# Revit family: DC_Holyoake_OutsideLouver_OHL-C-45_supply_13
name_source: partatom
category: Air Terminals
revit_build: Autodesk Revit 2014 (Build: 20130308_1515(x64)
units: mm (PartAtom-declared; Revit-internal decimal feet)

## types (1)
- OHL-C-45
    Accessories = Aluminium Bird mesh or insect mesh (fibreglass)
    Blade Array Count = 7.68
    Blade Count = 7
    Blade Cut Setout = 350 mm  [stored 1.14829 ft]
    Blade Height = 61.6 mm  [stored 0.2021 ft]
    Blade Length = 354 mm  [stored 1.16142 ft]
    Blade Offset = 3 mm  [stored 0.00984252 ft]
    Blade Pitch = 50 mm  [stored 0.164042 ft]
    Blade Setout = 384 mm
    Blade Width = 44.8 mm  [stored 0.146982 ft]
    Channel Thickness = 50.8 mm  [stored 0.166667 ft]
    Channel Width = 25.4 mm  [stored 0.0833333 ft]
    Description = Weather Louvres shall be Holyoake Model OHL-C-45 curved profile 45mm louvred blades set at 50mm centres and constructed in a channel (C) frame to suit the installation profile.  Weather Louvres shall be of extruded aluminium construction and finished in natural anodised or powdercoat and fitted with accessories and dampers where indicated as manufactured by Holyoake.
    Exact Neck Height = 390 mm  [stored 1.27953 ft]
    Exact Neck Width = 360 mm
    Exact Overall Channel Height = 438.2 mm
    Exact Overall Channel Width = 408.2 mm
    Holyoake Product Range = Outside Louvres
    Manufacturer = Holyoake
    Material - Body = Holyoake Aluminium
    Material - Face = Holyoake Aluminium
    Max Flow = 2000.0 L/s
    Min Flow = 100.0 L/s
    Model = OHL-C-45
    Noise Level NC Max = 0.00 NC
    Noise Level NC Min = 0.00 NC
    Nominal Height = 396 mm  [stored 1.29921 ft]
    Nominal Width = 366 mm
    Overall Opening Height = 366 mm
    Overall Opening Width = 336 mm
    Static Pressure Max = 0.0 Pa
    Static Pressure Min = 0.0 Pa
    Top Blade Height = 34 mm
    Type Comments = 45mm Horizontal Curved Profile Louvers in Channel Surround
    URL = http://www.holyoake.com

note: [stored X ft] marks values corroborated as IEEE doubles in the binary element streams (Revit-internal decimal feet)

## geometry (parser evidence)
native form markers: Blend x8, Sweep x8
no freeform markers — native parametric forms only
